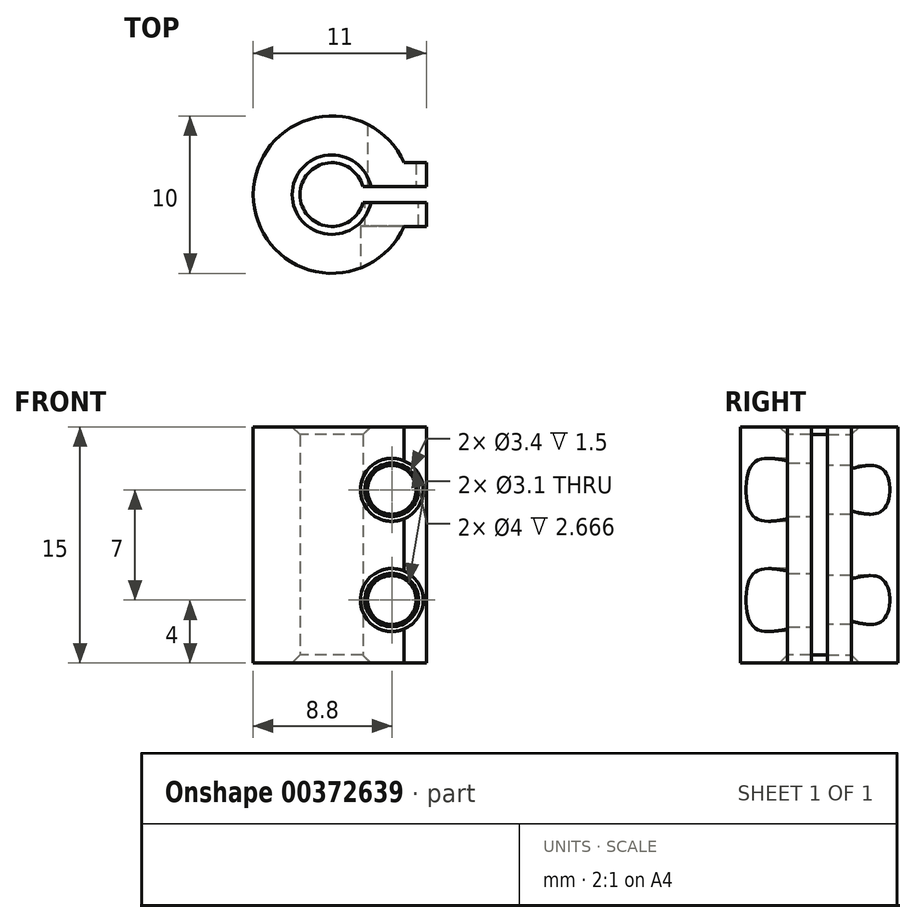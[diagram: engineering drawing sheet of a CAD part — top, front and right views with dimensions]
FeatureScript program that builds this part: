
annotation { "Feature Type Name" : "Feature", "Feature Type Description" : "" }
export const myFeature = defineFeature(function(context is Context, id is Id, definition is map)
    precondition{}
    {
        {
            var Q0;
            Q0=qCreatedBy(makeId("Top.planeOp"),FACE);
            var sketch = newSketch(context, id + "F0", { "sketchPlane" : qUnion([Q0])});
            skCircle(sketch, "E0", {"center": v(0, 0) * mm, "radius": 2.03 * mm});
            skCircle(sketch, "E1", {"center": v(0, 0) * mm, "radius": 5 * mm});
            skLineSegment(sketch, "E2.bottom", {"start": v(5.55, 0.5) * mm, "end": v(-1.5, 0.5) * mm});
            skLineSegment(sketch, "E2.top", {"start": v(5.55, -0.5) * mm, "end": v(-1.5, -0.5) * mm});
            skLineSegment(sketch, "E2.left", {"start": v(5.55, 0.5) * mm, "end": v(5.55, -0.5) * mm});
            skLineSegment(sketch, "E2.right", {"start": v(-1.5, 0.5) * mm, "end": v(-1.5, -0.5) * mm});
            skPoint(sketch, "E2.middle", {"position": v(2.03, 0) * mm});
            skLineSegment(sketch, "E3.bottom", {"start": v(0, 2.03) * mm, "end": v(6, 2.03) * mm});
            skLineSegment(sketch, "E3.top", {"start": v(0, 0.5) * mm, "end": v(6, 0.5) * mm});
            skLineSegment(sketch, "E3.left", {"start": v(0, 2.03) * mm, "end": v(0, 0.5) * mm});
            skLineSegment(sketch, "E3.right", {"start": v(6, 2.02) * mm, "end": v(6, 0.5) * mm});
            skLineSegment(sketch, "E4.bottom", {"start": v(0, -2.03) * mm, "end": v(6, -2.03) * mm});
            skLineSegment(sketch, "E4.top", {"start": v(0, -0.5) * mm, "end": v(6, -0.5) * mm});
            skLineSegment(sketch, "E4.left", {"start": v(0, -2.03) * mm, "end": v(0, -0.5) * mm});
            skLineSegment(sketch, "E4.right", {"start": v(6, -2.02) * mm, "end": v(6, -0.5) * mm});
            skSolve(sketch);
        }
        {
            var Q0;
            Q0=qCreatedBy(makeId("Front.planeOp"),FACE);
            var sketch = newSketch(context, id + "F1", { "sketchPlane" : qUnion([Q0])});
            skLineSegment(sketch, "E5", {"start": v(0, 0) * mm, "end": v(3.8, 0) * mm});
            skLineSegment(sketch, "E6", {"start": v(3.8, 0) * mm, "end": v(3.8, 4) * mm});
            skPoint(sketch, "E7.middle", {"position": v(3.8, 4) * mm});
            skCircle(sketch, "E8", {"center": v(3.8, 4) * mm, "radius": 1.55 * mm});
            skLineSegment(sketch, "E9", {"start": v(3.8, 4) * mm, "end": v(3.8, 11) * mm});
            skCircle(sketch, "E10", {"center": v(3.8, 11) * mm, "radius": 1.55 * mm});
            skCircle(sketch, "E11", {"center": v(3.8, 4) * mm, "radius": 1.7 * mm});
            skCircle(sketch, "E12", {"center": v(3.8, 11) * mm, "radius": 1.7 * mm});
            skSolve(sketch);
        }
        {
            var Q0;
            {var subQ0=sQuery(id+"F0.wireOp",EDGE,"E3.bottom");var subQ5=sQuery(id+"F0.wireOp",EDGE,"E1");var subQ6=makeQuery(id+"F0.imprint","INTERSECT",VERTEX,{"derivedFrom":[subQ5,subQ0]});Q0=makeQuery(id+"F0.imprint","IMPRINT",FACE,{"disambiguationData":[TD([[makeQuery(id+"F0.imprint","IMPRINT",EDGE,{"disambiguationData":[TD([[subQ6,-1.0]])],"derivedFrom":subQ5}),1.0]])]});}
            var Q1;
            {var subQ0=sQuery(id+"F0.wireOp",EDGE,"E3.bottom");var subQ5=sQuery(id+"F0.wireOp",EDGE,"E1");var subQ7=makeQuery(id+"F0.imprint","INTERSECT",VERTEX,{"derivedFrom":[subQ5,subQ0]});Q1=makeQuery(id+"F0.imprint","IMPRINT",FACE,{"disambiguationData":[TD([[makeQuery(id+"F0.imprint","IMPRINT",EDGE,{"disambiguationData":[TD([[subQ7,1.0]])],"derivedFrom":subQ5}),1.0]])]});}
            var Q2;
            {var subQ0=sQuery(id+"F0.wireOp",EDGE,"E4.bottom");var subQ5=sQuery(id+"F0.wireOp",EDGE,"E1");var subQ6=makeQuery(id+"F0.imprint","INTERSECT",VERTEX,{"derivedFrom":[subQ5,subQ0]});Q2=makeQuery(id+"F0.imprint","IMPRINT",FACE,{"disambiguationData":[TD([[makeQuery(id+"F0.imprint","IMPRINT",EDGE,{"disambiguationData":[TD([[subQ6,-1.0]])],"derivedFrom":subQ5}),1.0]])]});}
            var Q3;
            {var subQ2=sQuery(id+"F0.wireOp",EDGE,"E3.right");Q3=makeQuery(id+"F0.imprint","IMPRINT",FACE,{"disambiguationData":[TD([[makeQuery(id+"F0.imprint","IMPRINT",EDGE,{"derivedFrom":subQ2}),-1.0]])]});}
            var Q4;
            {var subQ2=sQuery(id+"F0.wireOp",EDGE,"E4.right");Q4=makeQuery(id+"F0.imprint","IMPRINT",FACE,{"disambiguationData":[TD([[makeQuery(id+"F0.imprint","IMPRINT",EDGE,{"derivedFrom":subQ2}),1.0]])]});}
            extrude(context, id + "F2", {"entities" : qUnion([Q0, Q1, Q2, Q3, Q4]), "depth" : 15 * mm});
        }
        {
            var Q0;
            Q0=makeQuery(id+"F1.imprint","IMPRINT",FACE,{"disambiguationData":[TD([[makeQuery(id+"F1.imprint","IMPRINT",EDGE,{"derivedFrom":sQuery(id+"F1.wireOp",EDGE,"E10")}),1.0]])]});
            var Q1;
            {var subQ0=sQuery(id+"F1.wireOp",EDGE,"E9");var subQ1=sQuery(id+"F1.wireOp",EDGE,"E6");var subQ2=makeQuery(id+"F1.imprint","INTERSECT",VERTEX,{"derivedFrom":[subQ1,subQ0]});Q1=makeQuery(id+"F1.imprint","IMPRINT",FACE,{"disambiguationData":[TD([[makeQuery(id+"F1.imprint","IMPRINT",EDGE,{"disambiguationData":[TD([[subQ2,1.0]])],"derivedFrom":subQ1}),-1.0]])]});}
            var Q2;
            {var subQ0=sQuery(id+"F1.wireOp",EDGE,"E9");var subQ1=sQuery(id+"F1.wireOp",EDGE,"E6");var subQ2=makeQuery(id+"F1.imprint","INTERSECT",VERTEX,{"derivedFrom":[subQ1,subQ0]});Q2=makeQuery(id+"F1.imprint","IMPRINT",FACE,{"disambiguationData":[TD([[makeQuery(id+"F1.imprint","IMPRINT",EDGE,{"disambiguationData":[TD([[subQ2,1.0]])],"derivedFrom":subQ1}),1.0]])]});}
            extrude(context, id + "F3", {"entities" : qUnion([Q0, Q1, Q2]), "operationType" : NewBodyOperationType.REMOVE, "oppositeDirection" : true, "depth" : 5 * mm});
        }
        {
            var Q0;
            Q0=makeQuery(id+"F1.imprint","IMPRINT",FACE,{"disambiguationData":[TD([[makeQuery(id+"F1.imprint","IMPRINT",EDGE,{"derivedFrom":sQuery(id+"F1.wireOp",EDGE,"E10")}),1.0]])]});
            var Q1;
            Q1=makeQuery(id+"F1.imprint","IMPRINT",FACE,{"disambiguationData":[TD([[makeQuery(id+"F1.imprint","IMPRINT",EDGE,{"derivedFrom":sQuery(id+"F1.wireOp",EDGE,"E10")}),-1.0]])]});
            var Q2;
            {var subQ0=sQuery(id+"F1.wireOp",EDGE,"E11");var subQ1=sQuery(id+"F1.wireOp",EDGE,"E6");var subQ2=makeQuery(id+"F1.imprint","INTERSECT",VERTEX,{"derivedFrom":[subQ1,subQ0]});Q2=makeQuery(id+"F1.imprint","IMPRINT",FACE,{"disambiguationData":[TD([[makeQuery(id+"F1.imprint","IMPRINT",EDGE,{"disambiguationData":[TD([[subQ2,-1.0]])],"derivedFrom":subQ1}),-1.0]])]});}
            var Q3;
            {var subQ0=sQuery(id+"F1.wireOp",EDGE,"E9");var subQ1=sQuery(id+"F1.wireOp",EDGE,"E6");var subQ2=makeQuery(id+"F1.imprint","INTERSECT",VERTEX,{"derivedFrom":[subQ1,subQ0]});Q3=makeQuery(id+"F1.imprint","IMPRINT",FACE,{"disambiguationData":[TD([[makeQuery(id+"F1.imprint","IMPRINT",EDGE,{"disambiguationData":[TD([[subQ2,1.0]])],"derivedFrom":subQ1}),-1.0]])]});}
            var Q4;
            {var subQ0=sQuery(id+"F1.wireOp",EDGE,"E9");var subQ1=sQuery(id+"F1.wireOp",EDGE,"E6");var subQ2=makeQuery(id+"F1.imprint","INTERSECT",VERTEX,{"derivedFrom":[subQ1,subQ0]});Q4=makeQuery(id+"F1.imprint","IMPRINT",FACE,{"disambiguationData":[TD([[makeQuery(id+"F1.imprint","IMPRINT",EDGE,{"disambiguationData":[TD([[subQ2,1.0]])],"derivedFrom":subQ1}),1.0]])]});}
            var Q5;
            {var subQ0=sQuery(id+"F1.wireOp",EDGE,"E11");var subQ1=sQuery(id+"F1.wireOp",EDGE,"E6");var subQ2=makeQuery(id+"F1.imprint","INTERSECT",VERTEX,{"derivedFrom":[subQ1,subQ0]});Q5=makeQuery(id+"F1.imprint","IMPRINT",FACE,{"disambiguationData":[TD([[makeQuery(id+"F1.imprint","IMPRINT",EDGE,{"disambiguationData":[TD([[subQ2,-1.0]])],"derivedFrom":subQ1}),1.0]])]});}
            extrude(context, id + "F4", {"entities" : qUnion([Q0, Q1, Q2, Q3, Q4, Q5]), "operationType" : NewBodyOperationType.REMOVE, "depth" : 5 * mm});
        }
        {
            var Q0;
            Q0=qCreatedBy(makeId("Front.planeOp"),FACE);
            cPlane(context, id + "F5", {"entities" : qUnion([Q0]), "cplaneType" : CPlaneType.OFFSET, "offset" : 5 * mm, "width" : 150 * mm, "height" : 150 * mm});
        }
        {
            var Q0;
            Q0=qCreatedBy(id+"F5.planeOp",FACE);
            var sketch = newSketch(context, id + "F6", { "sketchPlane" : qUnion([Q0])});
            skLineSegment(sketch, "E13", {"start": v(0, 0) * mm, "end": v(3.8, 0) * mm});
            skLineSegment(sketch, "E14", {"start": v(3.8, 0) * mm, "end": v(3.8, 4) * mm});
            skLineSegment(sketch, "E15", {"start": v(3.8, 4) * mm, "end": v(3.8, 11) * mm});
            skCircle(sketch, "E16", {"center": v(3.8, 4) * mm, "radius": 2 * mm});
            skCircle(sketch, "E17", {"center": v(3.8, 11) * mm, "radius": 2 * mm});
            skSolve(sketch);
        }
        {
            var Q0;
            Q0=makeQuery(id+"F6.imprint","IMPRINT",FACE,{"disambiguationData":[TD([[makeQuery(id+"F6.imprint","IMPRINT",EDGE,{"derivedFrom":sQuery(id+"F6.wireOp",EDGE,"E17")}),1.0]])]});
            var Q1;
            {var subQ0=sQuery(id+"F6.wireOp",EDGE,"E15");var subQ1=sQuery(id+"F6.wireOp",EDGE,"E14");var subQ2=makeQuery(id+"F6.imprint","INTERSECT",VERTEX,{"derivedFrom":[subQ1,subQ0]});Q1=makeQuery(id+"F6.imprint","IMPRINT",FACE,{"disambiguationData":[TD([[makeQuery(id+"F6.imprint","IMPRINT",EDGE,{"disambiguationData":[TD([[subQ2,1.0]])],"derivedFrom":subQ1}),1.0]])]});}
            var Q2;
            {var subQ0=sQuery(id+"F6.wireOp",EDGE,"E15");var subQ1=sQuery(id+"F6.wireOp",EDGE,"E14");var subQ2=makeQuery(id+"F6.imprint","INTERSECT",VERTEX,{"derivedFrom":[subQ1,subQ0]});Q2=makeQuery(id+"F6.imprint","IMPRINT",FACE,{"disambiguationData":[TD([[makeQuery(id+"F6.imprint","IMPRINT",EDGE,{"disambiguationData":[TD([[subQ2,1.0]])],"derivedFrom":subQ1}),-1.0]])]});}
            extrude(context, id + "F7", {"entities" : qUnion([Q0, Q1, Q2]), "operationType" : NewBodyOperationType.REMOVE, "oppositeDirection" : true, "depth" : 3 * mm});
        }
        {
            var Q0;
            Q0=makeQuery(id+"F2.opExtrude","CAP_EDGE",EDGE,{"disambiguationData":[OSD([sQuery(id+"F0.wireOp",EDGE,"E0")])],"isStart":false});
            var Q1;
            Q1=makeQuery(id+"F2.opExtrude","CAP_EDGE",EDGE,{"disambiguationData":[OSD([sQuery(id+"F0.wireOp",EDGE,"E0")])],"isStart":true});
            chamfer(context, id + "F8", {"entities" : qUnion([Q0, Q1]), "width" : .5 * mm, "tangentPropagation" : true});
        }
    });
